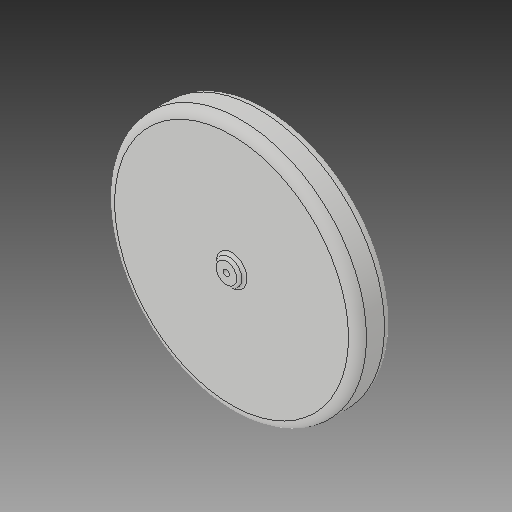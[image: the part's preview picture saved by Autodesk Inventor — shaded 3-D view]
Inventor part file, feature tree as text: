
AUTODESK INVENTOR PART (.ipt)
format: ipt  version: 2018 (Build 220112000, 112)  size: 164,352 bytes
history: native  units: mm
features: sketch x5, fillet x4, extrude x3, hole x2, other x1
ambient origin geometry x8: Origin, YZ Plane, XZ Plane, XY Plane, X Axis, Y Axis, Z Axis, Center Point
bodies: Body1 (feature_tree)
feature tree (15):
  other  "ソリッド1"
  extrude  "押し出し1"  Depth=490.0mm
  fillet  "フィレット1"  Radius=70.0mm
  extrude  "押し出し2"  Depth=17.5mm
  extrude  "押し出し3"  Depth=50.0mm
  fillet  "フィレット2"  Radius=10.0mm
  fillet  "フィレット3"  Radius=240.0mm
  fillet  "フィレット4"  Radius=35.0mm
  hole  "穴2"  [1 undecoded]
  hole  "穴3"  [1 undecoded]
  sketch  "スケッチ1"
  sketch  "スケッチ8"
  sketch  "スケッチ9"
  sketch  "スケッチ10"
  sketch  "スケッチ11"
note: 2 required parameter values undecoded (feature->parameter linkage not recoverable at this tier; creation-order binding heuristic only, values carry confidence <= 0.55)
